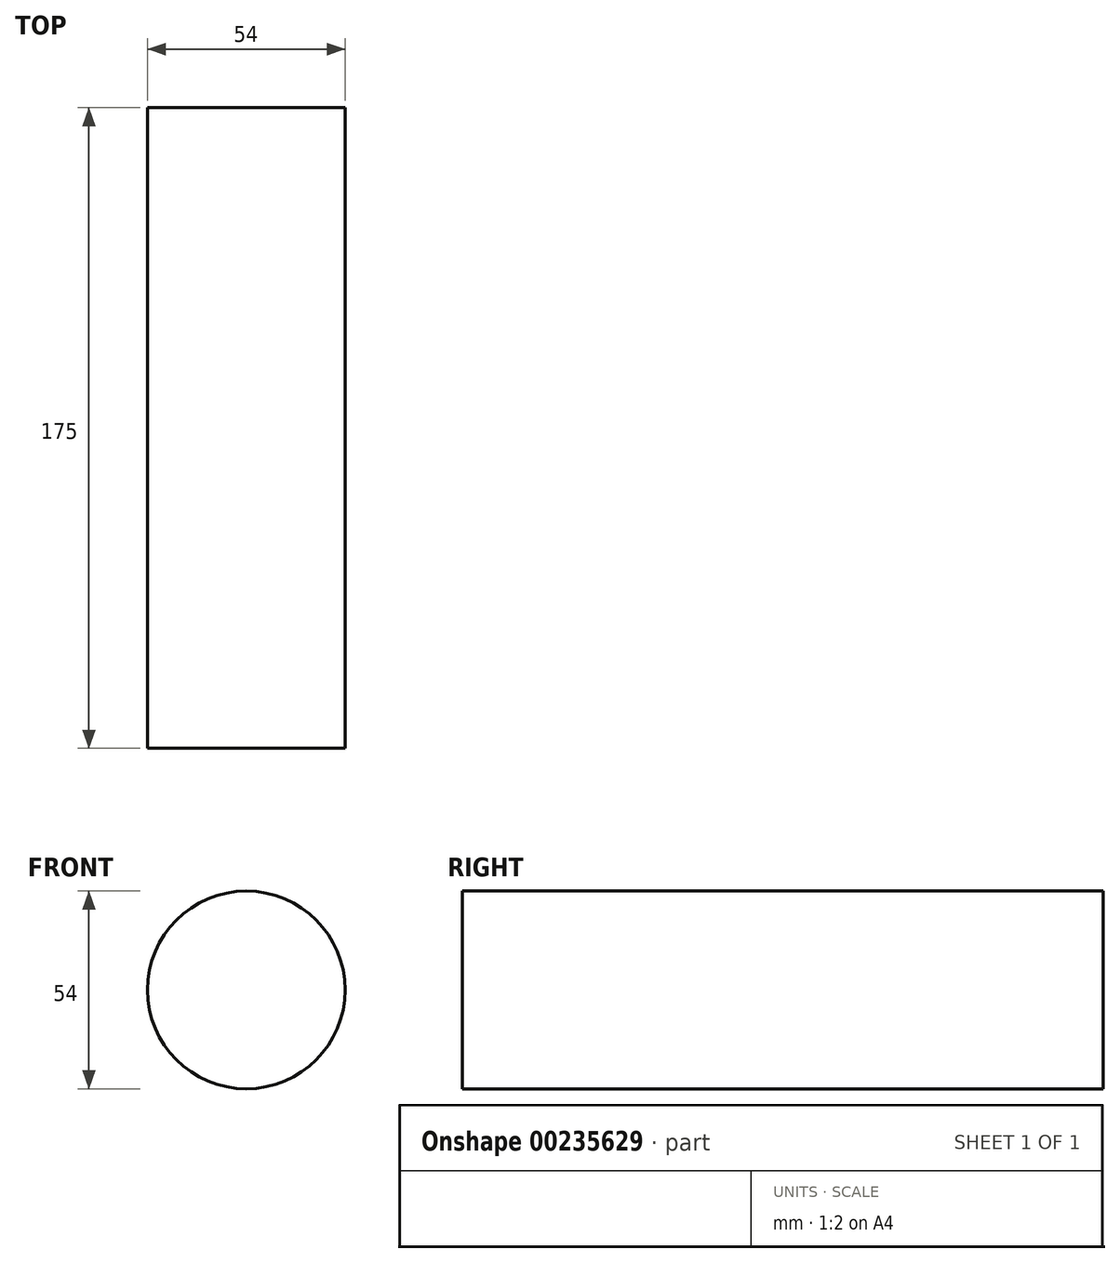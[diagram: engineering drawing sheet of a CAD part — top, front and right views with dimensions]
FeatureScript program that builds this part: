
annotation { "Feature Type Name" : "Feature", "Feature Type Description" : "" }
export const myFeature = defineFeature(function(context is Context, id is Id, definition is map)
    precondition{}
    {
        {
            var Q0;
            Q0=qCreatedBy(makeId("Front.planeOp"),FACE);
            var sketch = newSketch(context, id + "F0", { "sketchPlane" : qUnion([Q0])});
            skCircle(sketch, "E0", {"center": v(0, 0) * mm, "radius": 27 * mm});
            skSolve(sketch);
        }
        {
            var Q0;
            Q0=qSketchRegion(id+"F0",true);
            extrude(context, id + "F1", {"entities" : qUnion([Q0]), "depth" : 175 * mm});
        }
    });
